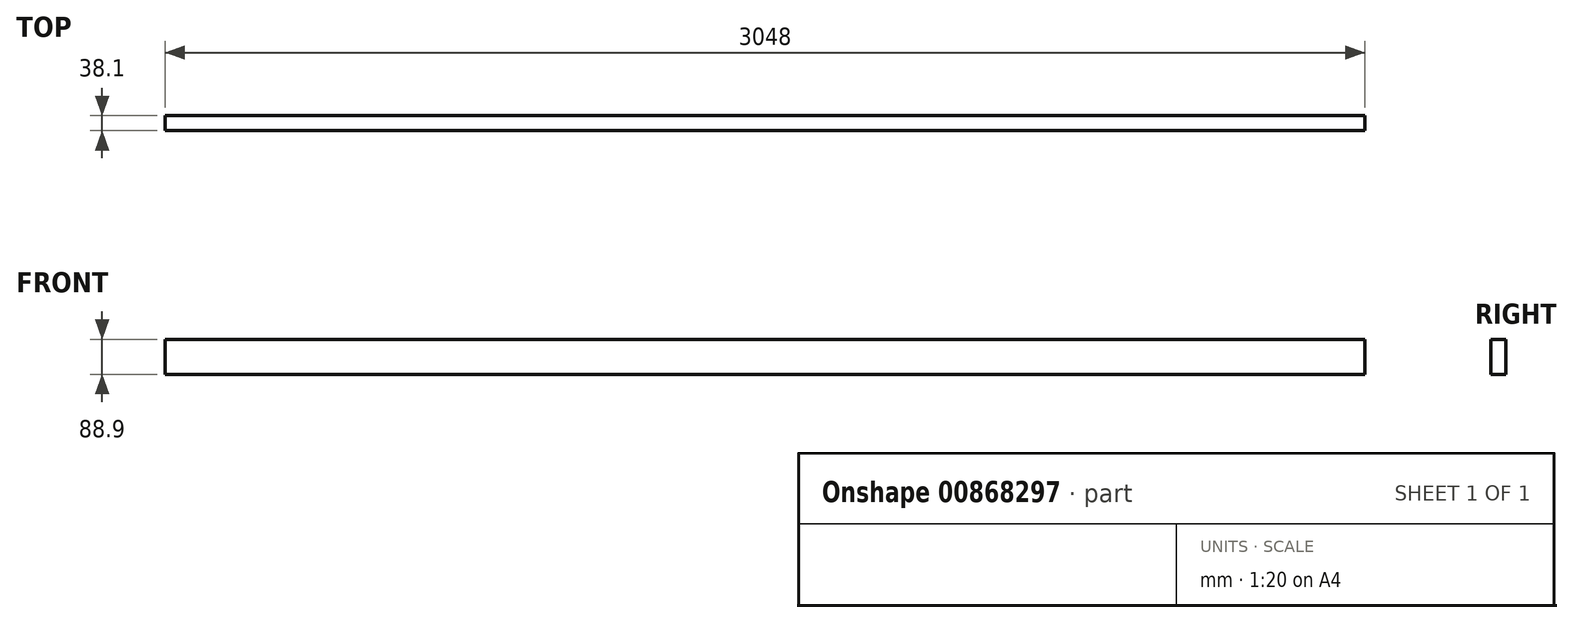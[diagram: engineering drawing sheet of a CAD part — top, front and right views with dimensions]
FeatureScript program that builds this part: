
annotation { "Feature Type Name" : "Feature", "Feature Type Description" : "" }
export const myFeature = defineFeature(function(context is Context, id is Id, definition is map)
    precondition{}
    {
        {
            var Q0;
            Q0=qCreatedBy(makeId("Right.planeOp"),FACE);
            var sketch = newSketch(context, id + "F0", { "sketchPlane" : qUnion([Q0])});
            skLineSegment(sketch, "E0.bottom", {"start": v(-138.83, 119.17) * mm, "end": v(-100.73, 119.17) * mm});
            skLineSegment(sketch, "E0.top", {"start": v(-138.83, 30.27) * mm, "end": v(-100.73, 30.27) * mm});
            skLineSegment(sketch, "E0.left", {"start": v(-138.83, 119.17) * mm, "end": v(-138.83, 30.27) * mm});
            skLineSegment(sketch, "E0.right", {"start": v(-100.73, 119.17) * mm, "end": v(-100.73, 30.27) * mm});
            skSolve(sketch);
        }
        {
            var Q0;
            Q0 = qSketchRegion(id + "F0", true);
            extrude(context, id + "F1", {"entities" : qUnion([Q0]), "depth" : 3048 * mm, "offsetDistance" : 25.4 * mm});
        }
    });
